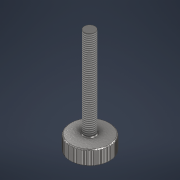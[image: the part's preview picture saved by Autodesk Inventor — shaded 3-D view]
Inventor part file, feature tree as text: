
AUTODESK INVENTOR PART (.ipt)
format: ipt  version: 2022 (Build 260153000, 153)  size: 508,416 bytes
history: native  units: mm
features: extrude x3, sketch x3, chamfer x2, thread x1, pattern_circular x1
ambient origin geometry x8: Origin, YZ Plane, XZ Plane, XY Plane, X Axis, Y Axis, Z Axis, Center Point
bodies: Solid1 (feature_tree)
feature tree (10):
  extrude  "Extrusion1"  Depth=4.0mm TaperAngle=0.0deg
  extrude  "Extrusion2"  Depth=25.0mm TaperAngle=0.0deg
  chamfer  "Chamfer1"  Distance=0.25mm Angle=45.0deg
  thread  "Thread1"  [1 undecoded]
  sketch  "Sketch3"  dims[d11=0.25mm d12=0.05mm d13=0.25mm d14=2.0mm d15=45.0deg d16=0.0mm d17=0.0mm d18=500.0mm d19=360.0deg]
  chamfer  "Chamfer2"  Distance=0.05mm
  extrude  "Extrusion3"  Depth=0.05mm TaperAngle=45.0deg
  pattern_circular  "Circular Pattern1"  [2 undecoded]
  sketch  "Sketch1"  dims[d0=11.0mm d1=4.0mm d2=0.0mm]
  sketch  "Sketch2"  dims[d3=3.0mm d4=25.0mm d5=0.0mm d6=0.25mm d7=2.0mm d8=45.0deg d9=24.75mm d10=0.0mm]
note: 3 required parameter values undecoded (feature->parameter linkage not recoverable at this tier; creation-order binding heuristic only, values carry confidence <= 0.55)
